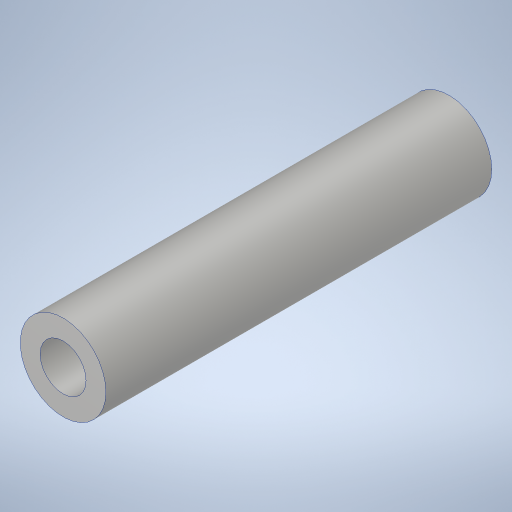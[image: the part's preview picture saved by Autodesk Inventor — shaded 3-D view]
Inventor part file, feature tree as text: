
AUTODESK INVENTOR PART (.ipt)
format: ipt  version: 2023.3 (Build 273359000, 359)  size: 233,472 bytes
history: native  units: in
note: dims shown in document units (in); Inventor stores cm internally (conversion verified against a paired STEP export)
features: sketch x1, extrude x1, hole x1
ambient origin geometry x8: Origin, YZ Plane, XZ Plane, XY Plane, X Axis, Y Axis, Z Axis, Center Point
bodies: Solid1 (feature_tree)
feature tree (3):
  sketch  "Sketch1"  dims[d1=1.688in d2=0.0in d3=0.201in d4=0.75in d5=0.385in d6=0.25in d7=0.5635in d8=1.0in d9=0.8108in d10=0.375in]
  extrude  "Extrusion1"  TaperAngle=0.0deg  [1 undecoded]
  hole  "Hole1"  [1 undecoded]
note: 2 required parameter values undecoded (feature->parameter linkage not recoverable at this tier; creation-order binding heuristic only, values carry confidence <= 0.55)
